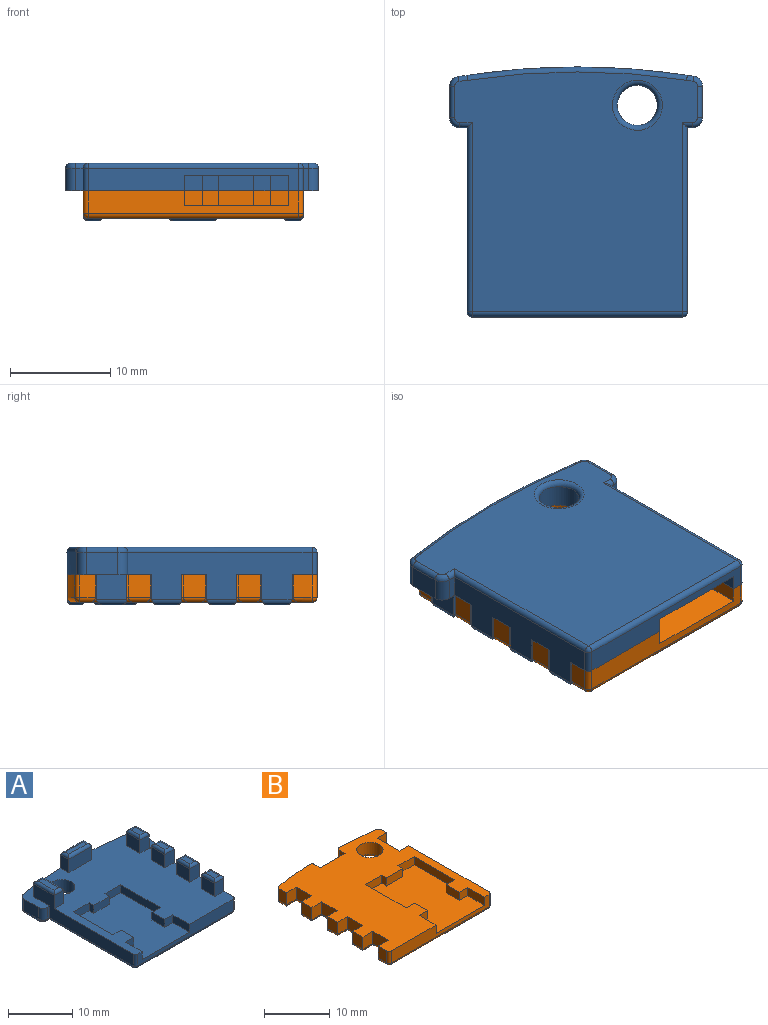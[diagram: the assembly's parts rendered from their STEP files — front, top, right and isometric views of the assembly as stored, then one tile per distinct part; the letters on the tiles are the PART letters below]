
ASSEMBLY  parts=2 mates=1
PART A: 103 faces, bbox 25.4x25.8x5.8 mm
  f0: plane 24.26x23.99mm, normal (0,0,-1), area 492.2mm2, adj f80,f82,f84,f85,f86,f87,f88,f89
  f1: plane 15.15x10.4mm, normal (0,0,1), area 144mm2, adj f8,f13,f14,f15,f16,f17,f18,f19
  f2: plane 2.25x0.88mm, normal (0.13,0.99,0), area 2mm2, adj f28,f91,f93,f95
  f3: cylinder r=72.71mm len=21.99mm, axis (0,0,1), area 62.2mm2, adj f4,f28,f50,f52,f75,f90,f93
  f4: plane 2.25x0.65mm, normal (-0.15,0.99,0), area 1.5mm2, adj f3,f28,f88,f101
  f5: plane 3.14x2.25mm, normal (-1,0,0), area 7.1mm2, adj f28,f86,f99,f101
  f6: plane 2.25x0.5mm, normal (0,-1,0), area 1.1mm2, adj f7,f28,f84,f99
  f7: plane 21.9x4.75mm, normal (-1,0,0), area 52.7mm2, adj f6,f28,f29,f31,f70,f78,f82
  f8: plane 21x2.25mm, normal (0,-1,0), area 31.7mm2, adj f1,f13,f27,f28,f78,f80,f81
  f9: plane 18.42x4.75mm, normal (1,0,0), area 63.9mm2, adj f10,f28,f33,f35,f42,f44,f46,f48
  f10: plane 2.25x0.76mm, normal (0,-1,0), area 1.7mm2, adj f9,f28,f87,f97
  f11: cylinder r=2mm len=4mm, axis (0,0,1), area 28.3mm2, adj f28,f94
  f12: plane 3.12x2.25mm, normal (1,0,0), area 7mm2, adj f28,f89,f95,f97
  f13: plane 3.65x1.5mm, normal (1,0,0), area 5.5mm2, adj f1,f8,f14,f28
  f14: plane 1.8x1.5mm, normal (0,-1,0), area 2.7mm2, adj f1,f13,f15,f28
  f15: plane 2.8x1.5mm, normal (1,0,0), area 4.2mm2, adj f1,f14,f16,f28
  f16: plane 1.8x1.5mm, normal (0,1,0), area 2.7mm2, adj f1,f15,f17,f28
  f17: plane 8.7x1.5mm, normal (1,0,0), area 13mm2, adj f1,f16,f18,f28
  f18: plane 3.45x1.5mm, normal (0,-1,0), area 5.2mm2, adj f1,f17,f19,f28
  f19: plane 1.5x1mm, normal (-1,0,0), area 1.5mm2, adj f1,f18,f20,f28
  f20: plane 3.5x1.5mm, normal (0,-1,0), area 5.2mm2, adj f1,f19,f21,f28
  f21: plane 1.5x1mm, normal (1,0,0), area 1.5mm2, adj f1,f20,f22,f28
  f22: plane 3.45x1.5mm, normal (0,-1,0), area 5.2mm2, adj f1,f21,f23,f28
  f23: plane 8.7x1.5mm, normal (-1,0,0), area 13mm2, adj f1,f22,f24,f28
  f24: plane 1.8x1.5mm, normal (0,1,0), area 2.7mm2, adj f1,f23,f25,f28
  f25: plane 2.8x1.5mm, normal (-1,0,0), area 4.2mm2, adj f1,f24,f26,f28
  f26: plane 1.8x1.5mm, normal (0,-1,0), area 2.7mm2, adj f1,f25,f27,f28
  f27: plane 3.65x1.5mm, normal (-1,0,0), area 5.5mm2, adj f1,f8,f26,f28
  f28: plane 25.26x24.94mm, normal (0,0,1), area 360.8mm2, adj f2,f3,f4,f5,f6,f7,f8,f9
  f29: plane 2.5x2mm, normal (0,-1,0), area 5mm2, adj f7,f28,f30,f71
  f30: plane 4.5x2.5mm, normal (1,0,0), area 11.2mm2, adj f28,f29,f31,f73
  f31: plane 2.5x2mm, normal (0,1,0), area 5mm2, adj f7,f28,f30,f72
  f32: plane 3.5x1mm, normal (0,0,1), area 3.5mm2, adj f70,f71,f72,f73
  f33: plane 2.5x2mm, normal (0,1,0), area 5mm2, adj f9,f28,f34,f57
  f34: plane 3x2.5mm, normal (-1,0,0), area 7.5mm2, adj f28,f33,f35,f55
  f35: plane 2.5x2mm, normal (0,-1,0), area 5mm2, adj f9,f28,f34,f54
  f36: plane 2x1mm, normal (0,0,1), area 2mm2, adj f54,f55,f56,f57
  f37: plane 3x2.5mm, normal (1,0,0), area 7.5mm2, adj f28,f38,f40,f68
  f38: plane 2.5x2mm, normal (0,1,0), area 5mm2, adj f28,f37,f39,f69
  f39: plane 3x2.5mm, normal (-1,0,0), area 7.5mm2, adj f28,f38,f40,f67
  f40: plane 2.5x2mm, normal (0,-1,0), area 5mm2, adj f28,f37,f39,f66
  f41: plane 2x1mm, normal (0,0,1), area 2mm2, adj f66,f67,f68,f69
  f42: plane 2.5x2mm, normal (0,1,0), area 5mm2, adj f9,f28,f43,f61
  f43: plane 3x2.5mm, normal (-1,0,0), area 7.5mm2, adj f28,f42,f44,f59
  f44: plane 2.5x2mm, normal (0,-1,0), area 5mm2, adj f9,f28,f43,f58
  f45: plane 2x1mm, normal (0,0,1), area 2mm2, adj f58,f59,f60,f61
  f46: plane 2.5x2mm, normal (0,1,0), area 5mm2, adj f9,f28,f47,f65
  f47: plane 3x2.5mm, normal (-1,0,0), area 7.5mm2, adj f28,f46,f48,f64
  f48: plane 2.5x2mm, normal (0,-1,0), area 5mm2, adj f9,f28,f47,f62
  f49: plane 2x1mm, normal (0,0,1), area 2mm2, adj f62,f63,f64,f65
  f50: plane 2.5x1.79mm, normal (-1,0,0), area 4.5mm2, adj f3,f28,f51,f77
  f51: plane 5x2.5mm, normal (0,-1,0), area 12.5mm2, adj f28,f50,f52,f76
  f52: plane 2.5x1.79mm, normal (1,0,0), area 4.5mm2, adj f3,f28,f51,f74
  f53: plane 4x0.84mm, normal (0,0,1), area 3.3mm2, adj f74,f75,f76,f77
  f54: cylinder r=0.5mm len=2mm, axis (-1,0,0), area 1.3mm2, adj f35,f36,f55,f56
  f55: cylinder r=0.5mm len=3mm, axis (0,1,0), area 2.1mm2, adj f34,f36,f54,f57
  f56: cylinder r=0.5mm len=3mm, axis (0,1,0), area 2.1mm2, adj f9,f36,f54,f57
  f57: cylinder r=0.5mm len=2mm, axis (1,0,0), area 1.3mm2, adj f33,f36,f55,f56
  f58: cylinder r=0.5mm len=2mm, axis (-1,0,0), area 1.3mm2, adj f44,f45,f59,f60
  f59: cylinder r=0.5mm len=3mm, axis (0,1,0), area 2.1mm2, adj f43,f45,f58,f61
  f60: cylinder r=0.5mm len=3mm, axis (0,1,0), area 2.1mm2, adj f9,f45,f58,f61
  f61: cylinder r=0.5mm len=2mm, axis (1,0,0), area 1.3mm2, adj f42,f45,f59,f60
  f62: cylinder r=0.5mm len=2mm, axis (-1,0,0), area 1.3mm2, adj f48,f49,f63,f64
  f63: cylinder r=0.5mm len=3mm, axis (0,1,0), area 2.1mm2, adj f9,f49,f62,f65
  f64: cylinder r=0.5mm len=3mm, axis (0,1,0), area 2.1mm2, adj f47,f49,f62,f65
  f65: cylinder r=0.5mm len=2mm, axis (1,0,0), area 1.3mm2, adj f46,f49,f63,f64
  f66: cylinder r=0.5mm len=2mm, axis (-1,0,0), area 1.3mm2, adj f40,f41,f67,f68
  f67: cylinder r=0.5mm len=3mm, axis (0,1,0), area 2.1mm2, adj f39,f41,f66,f69
  f68: cylinder r=0.5mm len=3mm, axis (0,-1,0), area 2.1mm2, adj f37,f41,f66,f69
  f69: cylinder r=0.5mm len=2mm, axis (1,0,0), area 1.3mm2, adj f38,f41,f67,f68
  f70: cylinder r=0.5mm len=4.5mm, axis (0,-1,0), area 3.2mm2, adj f7,f32,f71,f72
  f71: cylinder r=0.5mm len=2mm, axis (-1,0,0), area 1.3mm2, adj f29,f32,f70,f73
  f72: cylinder r=0.5mm len=2mm, axis (1,0,0), area 1.3mm2, adj f31,f32,f70,f73
  f73: cylinder r=0.5mm len=4.5mm, axis (0,-1,0), area 3.2mm2, adj f30,f32,f71,f72
  f74: cylinder r=0.5mm len=1.79mm, axis (0,-1,0), area 1.1mm2, adj f52,f53,f75,f76
  f75: torus R=72.21mm, axis (0,0,1), area 3.6mm2, adj f3,f53,f74,f77
  f76: cylinder r=0.5mm len=5mm, axis (-1,0,0), area 3.6mm2, adj f51,f53,f74,f77
  f77: cylinder r=0.5mm len=1.79mm, axis (0,1,0), area 1.1mm2, adj f50,f53,f75,f76
  f78: cylinder r=0.5mm len=2.25mm, axis (0,0,1), area 1.8mm2, adj f7,f8,f28,f79
  f79: sphere r=0.5mm, area 0.4mm2, adj f78,f80,f82
  f80: cylinder r=0.5mm len=21mm, axis (-1,0,0), area 16.5mm2, adj f0,f8,f79,f83
  f81: cylinder r=0.5mm len=2.25mm, axis (0,0,-1), area 1.8mm2, adj f8,f9,f28,f83
  f82: cylinder r=0.5mm len=18.92mm, axis (0,1,0), area 14.6mm2, adj f0,f7,f79,f84
  f83: sphere r=0.5mm, area 0.4mm2, adj f80,f81,f85
  f84: cylinder r=0.5mm len=1mm, axis (-1,0,0), area 0.5mm2, adj f0,f6,f82,f100
  f85: cylinder r=0.5mm len=18.92mm, axis (0,-1,0), area 14.6mm2, adj f0,f9,f83,f87
  f86: cylinder r=0.5mm len=3.14mm, axis (0,1,0), area 2.5mm2, adj f0,f5,f100,f102
  f87: cylinder r=0.5mm len=1.26mm, axis (-1,0,0), area 0.7mm2, adj f0,f10,f85,f98
  f88: cylinder r=0.5mm len=0.73mm, axis (0.99,0.15,0), area 0.5mm2, adj f0,f4,f90,f102
  f89: cylinder r=0.5mm len=3.12mm, axis (0,-1,0), area 2.5mm2, adj f0,f12,f96,f98
  f90: torus R=72.21mm, axis (0,0,1), area 17.3mm2, adj f0,f3,f88,f92
  f91: cylinder r=0.5mm len=0.95mm, axis (0.99,-0.13,0), area 0.7mm2, adj f0,f2,f92,f96
  f92: torus R=1mm, axis (0,0,1), area 0mm2, adj f0,f90,f91,f93
  f93: cylinder r=0.5mm len=2.25mm, axis (0,0,1), area 0mm2, adj f2,f3,f28,f92
  f94: torus R=2.5mm, axis (0,0,1), area 10.8mm2, adj f0,f11
  f95: cylinder r=1mm len=2.25mm, axis (0,0,-1), area 3.2mm2, adj f2,f12,f28,f96
  f96: torus R=0.5mm, axis (0,0,1), area 0.9mm2, adj f0,f89,f91,f95
  f97: cylinder r=1mm len=2.25mm, axis (0,0,1), area 3.5mm2, adj f10,f12,f28,f98
  f98: torus R=0.5mm, axis (0,0,1), area 1mm2, adj f0,f87,f89,f97
  f99: cylinder r=1mm len=2.25mm, axis (0,0,1), area 3.5mm2, adj f5,f6,f28,f100
  f100: torus R=0.5mm, axis (0,0,1), area 1mm2, adj f0,f84,f86,f99
  f101: cylinder r=1mm len=2.25mm, axis (0,0,1), area 3.2mm2, adj f4,f5,f28,f102
  f102: torus R=0.5mm, axis (0,0,1), area 0.9mm2, adj f0,f86,f88,f101
PART B: 88 faces, bbox 22x25x2.8 mm
  f0: plane 15.15x10.4mm, normal (0,0,1), area 144mm2, adj f29,f31,f32,f33,f34,f35,f36,f37
  f1: plane 17.25x2.25mm, normal (1,0,0), area 38.8mm2, adj f2,f46,f83,f86
  f2: plane 2.25x2mm, normal (0,1,0), area 4.5mm2, adj f1,f3,f46,f81
  f3: plane 4.8x2.25mm, normal (1,0,0), area 10.8mm2, adj f2,f4,f46,f78
  f4: plane 2.25x2mm, normal (0,-1,0), area 4.5mm2, adj f3,f5,f46,f76
  f5: plane 2.25x1.17mm, normal (1,0,0), area 2.6mm2, adj f4,f46,f69,f74
  f6: cylinder r=72.71mm len=7.4mm, axis (0,0,1), area 16.7mm2, adj f46,f64,f69,f70
  f7: plane 2.25x1.27mm, normal (-1,0,0), area 2.9mm2, adj f8,f46,f64,f65
  f8: plane 5.3x2.25mm, normal (0,1,0), area 11.9mm2, adj f7,f9,f46,f62
  f9: plane 2.25x1.27mm, normal (1,0,0), area 2.9mm2, adj f8,f46,f55,f60
  f10: cylinder r=72.71mm len=7.4mm, axis (0,0,1), area 16.7mm2, adj f46,f50,f55,f56
  f11: plane 2.25x1.57mm, normal (-1,0,0), area 3.5mm2, adj f12,f46,f50,f51
  f12: plane 2.25x2.15mm, normal (0,-1,0), area 4.8mm2, adj f11,f13,f46,f48
  f13: plane 3.3x2.25mm, normal (-1,0,0), area 7.4mm2, adj f12,f14,f46,f47
  f14: plane 2.25x2.15mm, normal (0,1,0), area 4.8mm2, adj f13,f15,f46,f49
  f15: plane 2.25x2.2mm, normal (-1,0,0), area 5mm2, adj f14,f16,f46,f52
  f16: plane 2.25x2.15mm, normal (0,-1,0), area 4.8mm2, adj f15,f17,f46,f54
  f17: plane 3.3x2.25mm, normal (-1,0,0), area 7.4mm2, adj f16,f18,f46,f57
  f18: plane 2.25x2.15mm, normal (0,1,0), area 4.8mm2, adj f17,f19,f46,f59
  f19: plane 2.25x2.2mm, normal (-1,0,0), area 4.9mm2, adj f18,f20,f46,f61
  f20: plane 2.25x2.15mm, normal (0,-1,0), area 4.8mm2, adj f19,f21,f46,f63
  f21: plane 3.3x2.25mm, normal (-1,0,0), area 7.4mm2, adj f20,f22,f46,f66
  f22: plane 2.25x2.15mm, normal (0,1,0), area 4.8mm2, adj f21,f23,f46,f68
  f23: plane 2.25x2.2mm, normal (-1,0,0), area 5mm2, adj f22,f24,f46,f71
  f24: plane 2.25x2.15mm, normal (0,-1,0), area 4.8mm2, adj f23,f25,f46,f73
  f25: plane 3.3x2.25mm, normal (-1,0,0), area 7.4mm2, adj f24,f26,f46,f75
  f26: plane 2.25x2.15mm, normal (0,1,0), area 4.8mm2, adj f25,f27,f46,f77
  f27: plane 2.25x1.85mm, normal (-1,0,0), area 4.2mm2, adj f26,f46,f79,f80
  f28: cylinder r=2mm len=4mm, axis (0,0,1), area 28.3mm2, adj f46,f87
  f29: plane 21x2.25mm, normal (0,-1,0), area 31.7mm2, adj f0,f31,f45,f46,f80,f84,f86
  f30: plane 23.92x21mm, normal (0,0,-1), area 418.7mm2, adj f47,f48,f49,f51,f52,f54,f56,f57
  f31: plane 3.65x1.5mm, normal (1,0,0), area 5.5mm2, adj f0,f29,f32,f46
  f32: plane 1.8x1.5mm, normal (0,-1,0), area 2.7mm2, adj f0,f31,f33,f46
  f33: plane 2.8x1.5mm, normal (1,0,0), area 4.2mm2, adj f0,f32,f34,f46
  f34: plane 1.8x1.5mm, normal (0,1,0), area 2.7mm2, adj f0,f33,f35,f46
  f35: plane 8.7x1.5mm, normal (1,0,0), area 13mm2, adj f0,f34,f36,f46
  f36: plane 3.45x1.5mm, normal (0,-1,0), area 5.2mm2, adj f0,f35,f37,f46
  f37: plane 1.5x1mm, normal (-1,0,0), area 1.5mm2, adj f0,f36,f38,f46
  f38: plane 3.5x1.5mm, normal (0,-1,0), area 5.2mm2, adj f0,f37,f39,f46
  f39: plane 1.5x1mm, normal (1,0,0), area 1.5mm2, adj f0,f38,f40,f46
  f40: plane 3.45x1.5mm, normal (0,-1,0), area 5.2mm2, adj f0,f39,f41,f46
  f41: plane 8.7x1.5mm, normal (-1,0,0), area 13mm2, adj f0,f40,f42,f46
  f42: plane 1.8x1.5mm, normal (0,1,0), area 2.7mm2, adj f0,f41,f43,f46
  f43: plane 2.8x1.5mm, normal (-1,0,0), area 4.2mm2, adj f0,f42,f44,f46
  f44: plane 1.8x1.5mm, normal (0,-1,0), area 2.7mm2, adj f0,f43,f45,f46
  f45: plane 3.65x1.5mm, normal (-1,0,0), area 5.5mm2, adj f0,f29,f44,f46
  f46: plane 24.92x22mm, normal (0,0,1), area 339.1mm2, adj f1,f2,f3,f4,f5,f6,f7,f8
  f47: cylinder r=0.5mm len=4.3mm, axis (0,1,0), area 2.9mm2, adj f13,f30,f48,f49
  f48: cylinder r=0.5mm len=2.65mm, axis (-1,0,0), area 1.7mm2, adj f12,f30,f47,f51
  f49: cylinder r=0.5mm len=2.65mm, axis (1,0,0), area 1.7mm2, adj f14,f30,f47,f52
  f50: cylinder r=0.5mm len=2.25mm, axis (0,0,1), area 1.6mm2, adj f10,f11,f46,f53
  f51: cylinder r=0.5mm len=1.57mm, axis (0,1,0), area 1.1mm2, adj f11,f30,f48,f53
  f52: cylinder r=0.5mm len=2.2mm, axis (0,1,0), area 1.4mm2, adj f15,f30,f49,f54
  f53: sphere r=0.5mm, area 0.4mm2, adj f50,f51,f56
  f54: cylinder r=0.5mm len=2.65mm, axis (-1,0,0), area 1.7mm2, adj f16,f30,f52,f57
  f55: cylinder r=0.5mm len=2.25mm, axis (0,0,1), area 1.8mm2, adj f9,f10,f46,f58
  f56: torus R=72.21mm, axis (0,0,1), area 5.8mm2, adj f10,f30,f53,f58
  f57: cylinder r=0.5mm len=4.3mm, axis (0,1,0), area 2.9mm2, adj f17,f30,f54,f59
  f58: sphere r=0.5mm, area 0.4mm2, adj f55,f56,f60
  f59: cylinder r=0.5mm len=2.65mm, axis (1,0,0), area 1.7mm2, adj f18,f30,f57,f61
  f60: cylinder r=0.5mm len=1.77mm, axis (0,-1,0), area 1.1mm2, adj f9,f30,f58,f62
  f61: cylinder r=0.5mm len=2.2mm, axis (0,1,0), area 1.4mm2, adj f19,f30,f59,f63
  f62: cylinder r=0.5mm len=6.3mm, axis (1,0,0), area 4.4mm2, adj f8,f30,f60,f65
  f63: cylinder r=0.5mm len=2.65mm, axis (-1,0,0), area 1.7mm2, adj f20,f30,f61,f66
  f64: cylinder r=0.5mm len=2.25mm, axis (0,0,1), area 1.8mm2, adj f6,f7,f46,f67
  f65: cylinder r=0.5mm len=1.77mm, axis (0,1,0), area 1.1mm2, adj f7,f30,f62,f67
  f66: cylinder r=0.5mm len=4.3mm, axis (0,1,0), area 2.9mm2, adj f21,f30,f63,f68
  f67: sphere r=0.5mm, area 0.4mm2, adj f64,f65,f70
  f68: cylinder r=0.5mm len=2.65mm, axis (1,0,0), area 1.7mm2, adj f22,f30,f66,f71
  f69: cylinder r=0.5mm len=2.25mm, axis (0,0,1), area 1.6mm2, adj f5,f6,f46,f72
  f70: torus R=72.21mm, axis (0,0,1), area 5.8mm2, adj f6,f30,f67,f72
  f71: cylinder r=0.5mm len=2.2mm, axis (0,1,0), area 1.4mm2, adj f23,f30,f68,f73
  f72: sphere r=0.5mm, area 0.4mm2, adj f69,f70,f74
  f73: cylinder r=0.5mm len=2.65mm, axis (-1,0,0), area 1.7mm2, adj f24,f30,f71,f75
  f74: cylinder r=0.5mm len=1.17mm, axis (0,-1,0), area 0.8mm2, adj f5,f30,f72,f76
  f75: cylinder r=0.5mm len=4.3mm, axis (0,1,0), area 2.9mm2, adj f25,f30,f73,f77
  f76: cylinder r=0.5mm len=2.5mm, axis (-1,0,0), area 1.6mm2, adj f4,f30,f74,f78
  f77: cylinder r=0.5mm len=2.65mm, axis (1,0,0), area 1.7mm2, adj f26,f30,f75,f79
  f78: cylinder r=0.5mm len=5.8mm, axis (0,-1,0), area 4.1mm2, adj f3,f30,f76,f81
  f79: cylinder r=0.5mm len=1.85mm, axis (0,1,0), area 1.3mm2, adj f27,f30,f77,f82
  f80: cylinder r=0.5mm len=2.25mm, axis (0,0,-1), area 1.8mm2, adj f27,f29,f46,f82
  f81: cylinder r=0.5mm len=2.5mm, axis (1,0,0), area 1.6mm2, adj f2,f30,f78,f83
  f82: sphere r=0.5mm, area 0.4mm2, adj f79,f80,f84
  f83: cylinder r=0.5mm len=17.25mm, axis (0,-1,0), area 13.4mm2, adj f1,f30,f81,f85
  f84: cylinder r=0.5mm len=21mm, axis (-1,0,0), area 16.5mm2, adj f29,f30,f82,f85
  f85: sphere r=0.5mm, area 0.4mm2, adj f83,f84,f86
  f86: cylinder r=0.5mm len=2.25mm, axis (0,0,1), area 1.8mm2, adj f1,f29,f46,f85
  f87: torus R=2.5mm, axis (0,0,1), area 10.8mm2, adj f28,f30
PLACE A rot(axis=(0,1,0),180deg) t=(-6.5,-0.63,4.27)mm
PLACE B t=(-6.5,-0.63,1.27)mm
MATE fastened A.f11 <-> B.f28  axis (0,0,-1) through (15.49,6.71,2.77)mm
